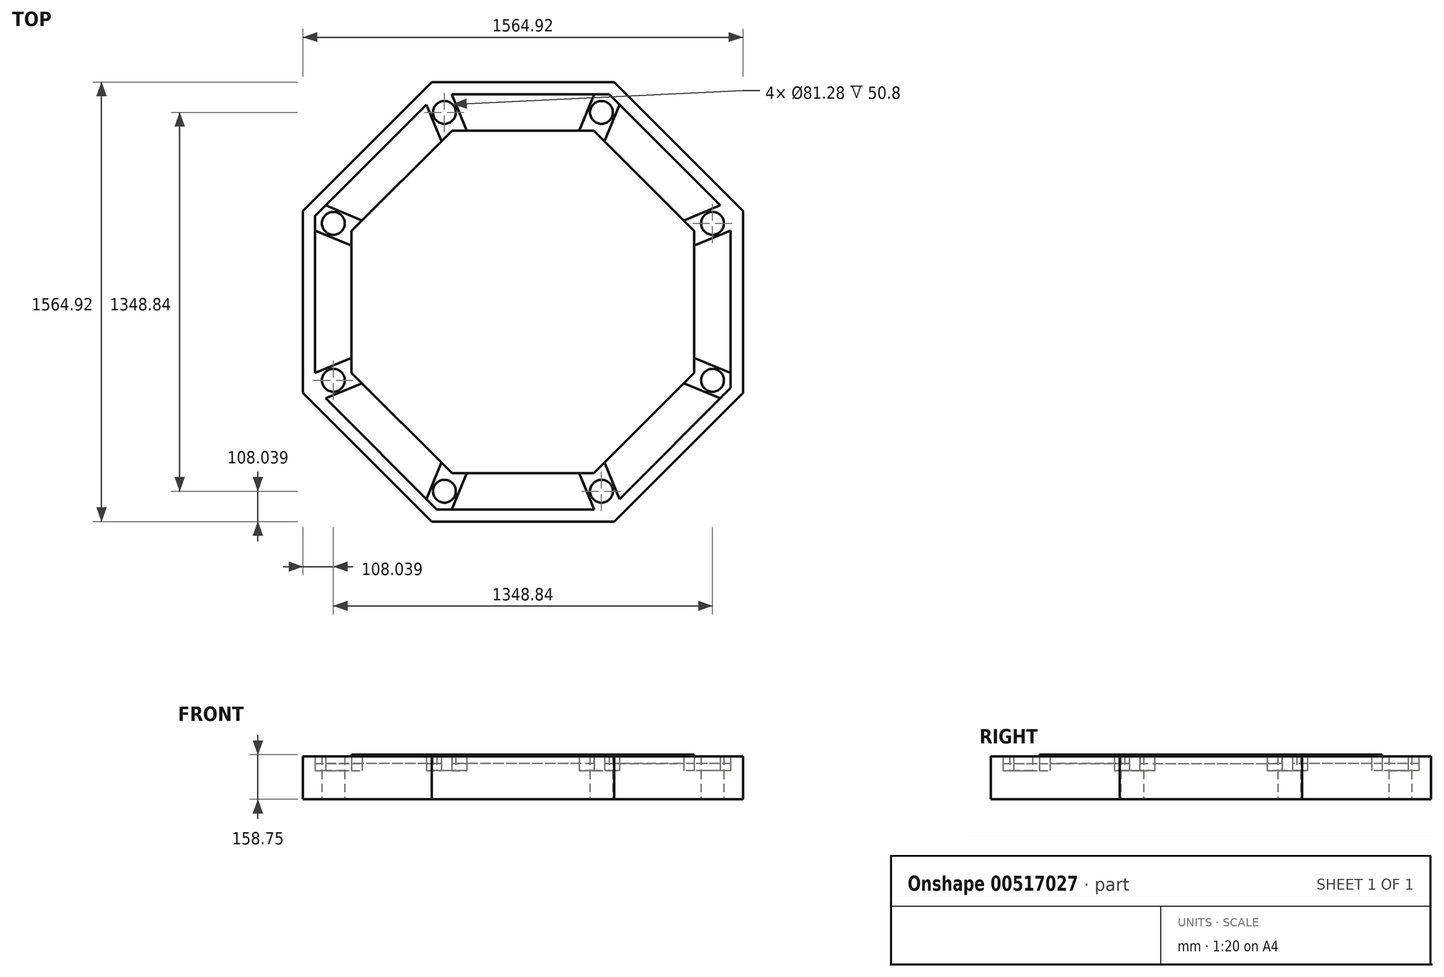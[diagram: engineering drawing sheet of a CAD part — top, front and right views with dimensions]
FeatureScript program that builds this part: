
annotation { "Feature Type Name" : "Feature", "Feature Type Description" : "" }
export const myFeature = defineFeature(function(context is Context, id is Id, definition is map)
    precondition{}
    {
        {
            var Q0;
            Q0=qCreatedBy(makeId("Top.planeOp"),FACE);
            var sketch = newSketch(context, id + "F0", { "sketchPlane" : qUnion([Q0])});
            skLineSegment(sketch, "E0.0", {"start": v(-324.1, 782.46) * mm, "end": v(324.1, 782.46) * mm});
            skLineSegment(sketch, "E0.1", {"start": v(324.1, 782.46) * mm, "end": v(782.46, 324.1) * mm});
            skLineSegment(sketch, "E0.2", {"start": v(782.46, 324.1) * mm, "end": v(782.46, -324.1) * mm});
            skLineSegment(sketch, "E0.3", {"start": v(782.46, -324.1) * mm, "end": v(324.1, -782.46) * mm});
            skLineSegment(sketch, "E0.4", {"start": v(324.1, -782.46) * mm, "end": v(-324.1, -782.46) * mm});
            skLineSegment(sketch, "E0.5", {"start": v(-324.1, -782.46) * mm, "end": v(-782.46, -324.1) * mm});
            skLineSegment(sketch, "E0.6", {"start": v(-782.46, -324.1) * mm, "end": v(-782.46, 324.1) * mm});
            skLineSegment(sketch, "E0.7", {"start": v(-782.46, 324.1) * mm, "end": v(-324.1, 782.46) * mm});
            skPoint(sketch, "E0.0.midPoint", {"position": v(0, 782.46) * mm});
            skLineSegment(sketch, "E1.0", {"start": v(-252.5, 609.6) * mm, "end": v(252.5, 609.6) * mm});
            skLineSegment(sketch, "E1.1", {"start": v(252.5, 609.6) * mm, "end": v(609.6, 252.5) * mm});
            skLineSegment(sketch, "E1.2", {"start": v(609.6, 252.5) * mm, "end": v(609.6, -252.5) * mm});
            skLineSegment(sketch, "E1.3", {"start": v(609.6, -252.5) * mm, "end": v(252.5, -609.6) * mm});
            skLineSegment(sketch, "E1.4", {"start": v(252.5, -609.6) * mm, "end": v(-252.5, -609.6) * mm});
            skLineSegment(sketch, "E1.5", {"start": v(-252.5, -609.6) * mm, "end": v(-609.6, -252.5) * mm});
            skLineSegment(sketch, "E1.6", {"start": v(-609.6, -252.5) * mm, "end": v(-609.6, 252.5) * mm});
            skLineSegment(sketch, "E1.7", {"start": v(-609.6, 252.5) * mm, "end": v(-252.5, 609.6) * mm});
            skPoint(sketch, "E1.0.midPoint", {"position": v(0, 609.6) * mm});
            skLineSegment(sketch, "E2.0", {"start": v(-306.2, 739.24) * mm, "end": v(306.2, 739.24) * mm});
            skLineSegment(sketch, "E2.1", {"start": v(306.2, 739.24) * mm, "end": v(739.24, 306.2) * mm});
            skLineSegment(sketch, "E2.2", {"start": v(739.24, 306.2) * mm, "end": v(739.24, -306.2) * mm});
            skLineSegment(sketch, "E2.3", {"start": v(739.24, -306.2) * mm, "end": v(306.2, -739.24) * mm});
            skLineSegment(sketch, "E2.4", {"start": v(306.2, -739.24) * mm, "end": v(-306.2, -739.24) * mm});
            skLineSegment(sketch, "E2.5", {"start": v(-306.2, -739.24) * mm, "end": v(-739.24, -306.2) * mm});
            skLineSegment(sketch, "E2.6", {"start": v(-739.24, -306.2) * mm, "end": v(-739.24, 306.2) * mm});
            skLineSegment(sketch, "E2.7", {"start": v(-739.24, 306.2) * mm, "end": v(-306.2, 739.24) * mm});
            skPoint(sketch, "E2.0.midPoint", {"position": v(0, 739.24) * mm});
            skLineSegment(sketch, "E3", {"start": v(-306.2, 739.24) * mm, "end": v(-252.5, 609.6) * mm, "construction": true});
            skLineSegment(sketch, "E4.0", {"start": v(-253.58, 739.24) * mm, "end": v(-199.88, 609.6) * mm});
            skLineSegment(sketch, "E5.0", {"start": v(-343.41, 702.03) * mm, "end": v(-289.71, 572.4) * mm});
            skLineSegment(sketch, "E6", {"start": v(0, 782.46) * mm, "end": v(0, -782.46) * mm, "construction": true});
            skCircle(sketch, "E7", {"center": v(-279.35, 674.42) * mm, "radius": 40.64 * mm});
            skLineSegment(sketch, "E8.MirrorCS", {"start": v(253.58, 739.24) * mm, "end": v(199.88, 609.6) * mm});
            skLineSegment(sketch, "E9.MirrorCS", {"start": v(343.41, 702.03) * mm, "end": v(289.71, 572.4) * mm});
            skCircle(sketch, "E10.MirrorC", {"center": v(279.35, 674.42) * mm, "radius": 40.64 * mm});
            skLineSegment(sketch, "E11", {"start": v(-782.46, 0) * mm, "end": v(782.46, 0) * mm, "construction": true});
            skLineSegment(sketch, "E12.MirrorCS", {"start": v(343.41, -702.03) * mm, "end": v(289.71, -572.4) * mm});
            skLineSegment(sketch, "E13.MirrorCS", {"start": v(253.58, -739.24) * mm, "end": v(199.88, -609.6) * mm});
            skCircle(sketch, "E14.MirrorC", {"center": v(279.35, -674.42) * mm, "radius": 40.64 * mm});
            skCircle(sketch, "E15.MirrorC", {"center": v(-279.35, -674.42) * mm, "radius": 40.64 * mm});
            skLineSegment(sketch, "E16.MirrorCS", {"start": v(-253.58, -739.24) * mm, "end": v(-199.88, -609.6) * mm});
            skLineSegment(sketch, "E17.MirrorCS", {"start": v(-343.41, -702.03) * mm, "end": v(-289.71, -572.4) * mm});
            skLineSegment(sketch, "E18", {"start": v(553.28, -553.28) * mm, "end": v(-553.28, 553.28) * mm, "construction": true});
            skLineSegment(sketch, "E19", {"start": v(553.28, 553.28) * mm, "end": v(-553.28, -553.28) * mm, "construction": true});
            skLineSegment(sketch, "E20.MirrorCS", {"start": v(702.03, 343.41) * mm, "end": v(572.4, 289.71) * mm});
            skLineSegment(sketch, "E21.MirrorCS", {"start": v(739.24, 253.58) * mm, "end": v(609.6, 199.88) * mm});
            skCircle(sketch, "E22.MirrorC", {"center": v(674.42, 279.35) * mm, "radius": 40.64 * mm});
            skLineSegment(sketch, "E23.MirrorCS", {"start": v(-739.24, -253.58) * mm, "end": v(-609.6, -199.88) * mm});
            skCircle(sketch, "E24.MirrorC", {"center": v(-674.42, -279.35) * mm, "radius": 40.64 * mm});
            skLineSegment(sketch, "E25.MirrorCS", {"start": v(-702.03, -343.41) * mm, "end": v(-572.4, -289.71) * mm});
            skLineSegment(sketch, "E26.MirrorCS", {"start": v(702.03, -343.41) * mm, "end": v(572.4, -289.71) * mm});
            skLineSegment(sketch, "E27.MirrorCS", {"start": v(739.24, -253.58) * mm, "end": v(609.6, -199.88) * mm});
            skCircle(sketch, "E28.MirrorC", {"center": v(674.42, -279.35) * mm, "radius": 40.64 * mm});
            skLineSegment(sketch, "E29.MirrorCS", {"start": v(-702.03, 343.41) * mm, "end": v(-572.4, 289.71) * mm});
            skLineSegment(sketch, "E30.MirrorCS", {"start": v(-739.24, 253.58) * mm, "end": v(-609.6, 199.88) * mm});
            skCircle(sketch, "E31.MirrorC", {"center": v(-674.42, 279.35) * mm, "radius": 40.64 * mm});
            skSolve(sketch);
        }
        {
            var Q0;
            Q0=makeQuery(id+"F0.imprint","IMPRINT",FACE,{"disambiguationData":[TD([[makeQuery(id+"F0.imprint","IMPRINT",EDGE,{"derivedFrom":sQuery(id+"F0.wireOp",EDGE,"E0.0")}),-1.0]])]});
            extrude(context, id + "F1", {"entities" : qUnion([Q0]), "endBound" : BoundingType.SYMMETRIC, "depth" : 152.4 * mm});
        }
        {
            var Q0;
            {var subQ0=sQuery(id+"F0.wireOp",EDGE,"E5.0");Q0=makeQuery(id+"F0.imprint","IMPRINT",FACE,{"disambiguationData":[TD([[makeQuery(id+"F0.imprint","IMPRINT",EDGE,{"derivedFrom":subQ0}),-1.0]])]});}
            var Q1;
            {var subQ0=sQuery(id+"F0.wireOp",EDGE,"E4.0");Q1=makeQuery(id+"F0.imprint","IMPRINT",FACE,{"disambiguationData":[TD([[makeQuery(id+"F0.imprint","IMPRINT",EDGE,{"derivedFrom":subQ0}),1.0]])]});}
            var Q2;
            {var subQ0=sQuery(id+"F0.wireOp",EDGE,"E9.MirrorCS");Q2=makeQuery(id+"F0.imprint","IMPRINT",FACE,{"disambiguationData":[TD([[makeQuery(id+"F0.imprint","IMPRINT",EDGE,{"derivedFrom":subQ0}),1.0]])]});}
            var Q3;
            {var subQ0=sQuery(id+"F0.wireOp",EDGE,"E23.MirrorCS");Q3=makeQuery(id+"F0.imprint","IMPRINT",FACE,{"disambiguationData":[TD([[makeQuery(id+"F0.imprint","IMPRINT",EDGE,{"derivedFrom":subQ0}),1.0]])]});}
            var Q4;
            {var subQ0=sQuery(id+"F0.wireOp",EDGE,"E21.MirrorCS");Q4=makeQuery(id+"F0.imprint","IMPRINT",FACE,{"disambiguationData":[TD([[makeQuery(id+"F0.imprint","IMPRINT",EDGE,{"derivedFrom":subQ0}),1.0]])]});}
            var Q5;
            {var subQ0=sQuery(id+"F0.wireOp",EDGE,"E12.MirrorCS");Q5=makeQuery(id+"F0.imprint","IMPRINT",FACE,{"disambiguationData":[TD([[makeQuery(id+"F0.imprint","IMPRINT",EDGE,{"derivedFrom":subQ0}),-1.0]])]});}
            var Q6;
            {var subQ0=sQuery(id+"F0.wireOp",EDGE,"E13.MirrorCS");Q6=makeQuery(id+"F0.imprint","IMPRINT",FACE,{"disambiguationData":[TD([[makeQuery(id+"F0.imprint","IMPRINT",EDGE,{"derivedFrom":subQ0}),1.0]])]});}
            var Q7;
            {var subQ0=sQuery(id+"F0.wireOp",EDGE,"E17.MirrorCS");Q7=makeQuery(id+"F0.imprint","IMPRINT",FACE,{"disambiguationData":[TD([[makeQuery(id+"F0.imprint","IMPRINT",EDGE,{"derivedFrom":subQ0}),1.0]])]});}
            extrude(context, id + "F2", {"entities" : qUnion([Q0, Q1, Q2, Q3, Q4, Q5, Q6, Q7]), "operationType" : NewBodyOperationType.ADD, "endBound" : BoundingType.SYMMETRIC, "depth" : 127 * mm});
        }
        {
            var Q0;
            Q0=makeQuery(id+"F2.opExtrude","CAP_FACE",FACE,{"disambiguationData":[OSD([sQuery(id+"F0.wireOp",EDGE,"E1.3"),sQuery(id+"F0.wireOp",EDGE,"E2.3"),sQuery(id+"F0.wireOp",EDGE,"E12.MirrorCS"),sQuery(id+"F0.wireOp",EDGE,"E26.MirrorCS")])],"isStart":true});
            var Q1;
            Q1=makeQuery(id+"F2.opExtrude","CAP_FACE",FACE,{"disambiguationData":[OSD([sQuery(id+"F0.wireOp",EDGE,"E1.4"),sQuery(id+"F0.wireOp",EDGE,"E2.4"),sQuery(id+"F0.wireOp",EDGE,"E13.MirrorCS"),sQuery(id+"F0.wireOp",EDGE,"E16.MirrorCS")])],"isStart":true});
            var Q2;
            Q2=makeQuery(id+"F2.opExtrude","CAP_FACE",FACE,{"disambiguationData":[OSD([sQuery(id+"F0.wireOp",EDGE,"E1.5"),sQuery(id+"F0.wireOp",EDGE,"E2.5"),sQuery(id+"F0.wireOp",EDGE,"E17.MirrorCS"),sQuery(id+"F0.wireOp",EDGE,"E25.MirrorCS")])],"isStart":true});
            var Q3;
            Q3=makeQuery(id+"F2.opExtrude","CAP_FACE",FACE,{"disambiguationData":[OSD([sQuery(id+"F0.wireOp",EDGE,"E1.6"),sQuery(id+"F0.wireOp",EDGE,"E2.6"),sQuery(id+"F0.wireOp",EDGE,"E23.MirrorCS"),sQuery(id+"F0.wireOp",EDGE,"E30.MirrorCS")])],"isStart":true});
            var Q4;
            Q4=makeQuery(id+"F2.opExtrude","CAP_FACE",FACE,{"disambiguationData":[OSD([sQuery(id+"F0.wireOp",EDGE,"E1.7"),sQuery(id+"F0.wireOp",EDGE,"E2.7"),sQuery(id+"F0.wireOp",EDGE,"E5.0"),sQuery(id+"F0.wireOp",EDGE,"E29.MirrorCS")])],"isStart":true});
            var Q5;
            Q5=makeQuery(id+"F2.opExtrude","CAP_FACE",FACE,{"disambiguationData":[OSD([sQuery(id+"F0.wireOp",EDGE,"E1.0"),sQuery(id+"F0.wireOp",EDGE,"E2.0"),sQuery(id+"F0.wireOp",EDGE,"E4.0"),sQuery(id+"F0.wireOp",EDGE,"E8.MirrorCS")])],"isStart":true});
            var Q6;
            Q6=makeQuery(id+"F2.opExtrude","CAP_FACE",FACE,{"disambiguationData":[OSD([sQuery(id+"F0.wireOp",EDGE,"E1.1"),sQuery(id+"F0.wireOp",EDGE,"E2.1"),sQuery(id+"F0.wireOp",EDGE,"E9.MirrorCS"),sQuery(id+"F0.wireOp",EDGE,"E20.MirrorCS")])],"isStart":true});
            var Q7;
            Q7=makeQuery(id+"F2.opExtrude","CAP_FACE",FACE,{"disambiguationData":[OSD([sQuery(id+"F0.wireOp",EDGE,"E1.2"),sQuery(id+"F0.wireOp",EDGE,"E2.2"),sQuery(id+"F0.wireOp",EDGE,"E21.MirrorCS"),sQuery(id+"F0.wireOp",EDGE,"E27.MirrorCS")])],"isStart":true});
            extrude(context, id + "F3", {"entities" : qUnion([Q0, Q1, Q2, Q3, Q4, Q5, Q6, Q7]), "operationType" : NewBodyOperationType.ADD, "depth" : 12.7 * mm});
        }
        {
            var Q0;
            {var subQ4=sQuery(id+"F0.wireOp",EDGE,"E4.0");Q0=makeQuery(id+"F0.imprint","IMPRINT",FACE,{"disambiguationData":[TD([[makeQuery(id+"F0.imprint","IMPRINT",EDGE,{"derivedFrom":subQ4}),-1.0]])]});}
            var Q1;
            {var subQ3=sQuery(id+"F0.wireOp",EDGE,"E8.MirrorCS");Q1=makeQuery(id+"F0.imprint","IMPRINT",FACE,{"disambiguationData":[TD([[makeQuery(id+"F0.imprint","IMPRINT",EDGE,{"derivedFrom":subQ3}),1.0]])]});}
            var Q2;
            {var subQ7=sQuery(id+"F0.wireOp",EDGE,"E29.MirrorCS");Q2=makeQuery(id+"F0.imprint","IMPRINT",FACE,{"disambiguationData":[TD([[makeQuery(id+"F0.imprint","IMPRINT",EDGE,{"derivedFrom":subQ7}),-1.0]])]});}
            var Q3;
            {var subQ4=sQuery(id+"F0.wireOp",EDGE,"E23.MirrorCS");Q3=makeQuery(id+"F0.imprint","IMPRINT",FACE,{"disambiguationData":[TD([[makeQuery(id+"F0.imprint","IMPRINT",EDGE,{"derivedFrom":subQ4}),-1.0]])]});}
            var Q4;
            {var subQ3=sQuery(id+"F0.wireOp",EDGE,"E20.MirrorCS");Q4=makeQuery(id+"F0.imprint","IMPRINT",FACE,{"disambiguationData":[TD([[makeQuery(id+"F0.imprint","IMPRINT",EDGE,{"derivedFrom":subQ3}),1.0]])]});}
            var Q5;
            {var subQ7=sQuery(id+"F0.wireOp",EDGE,"E26.MirrorCS");Q5=makeQuery(id+"F0.imprint","IMPRINT",FACE,{"disambiguationData":[TD([[makeQuery(id+"F0.imprint","IMPRINT",EDGE,{"derivedFrom":subQ7}),-1.0]])]});}
            var Q6;
            Q6=makeQuery(id+"F0.imprint","IMPRINT",FACE,{"disambiguationData":[TD([[makeQuery(id+"F0.imprint","IMPRINT",EDGE,{"derivedFrom":sQuery(id+"F0.wireOp",EDGE,"E15.MirrorC")}),1.0]])]});
            var Q7;
            {var subQ3=sQuery(id+"F0.wireOp",EDGE,"E12.MirrorCS");Q7=makeQuery(id+"F0.imprint","IMPRINT",FACE,{"disambiguationData":[TD([[makeQuery(id+"F0.imprint","IMPRINT",EDGE,{"derivedFrom":subQ3}),1.0]])]});}
            var Q8;
            Q8=makeQuery(id+"F0.imprint","IMPRINT",FACE,{"disambiguationData":[TD([[makeQuery(id+"F0.imprint","IMPRINT",EDGE,{"derivedFrom":sQuery(id+"F0.wireOp",EDGE,"E22.MirrorC")}),1.0]])]});
            var Q9;
            Q9=makeQuery(id+"F0.imprint","IMPRINT",FACE,{"disambiguationData":[TD([[makeQuery(id+"F0.imprint","IMPRINT",EDGE,{"derivedFrom":sQuery(id+"F0.wireOp",EDGE,"E10.MirrorC")}),-1.0]])]});
            var Q10;
            Q10=makeQuery(id+"F0.imprint","IMPRINT",FACE,{"disambiguationData":[TD([[makeQuery(id+"F0.imprint","IMPRINT",EDGE,{"derivedFrom":sQuery(id+"F0.wireOp",EDGE,"E7")}),1.0]])]});
            var Q11;
            Q11=makeQuery(id+"F0.imprint","IMPRINT",FACE,{"disambiguationData":[TD([[makeQuery(id+"F0.imprint","IMPRINT",EDGE,{"derivedFrom":sQuery(id+"F0.wireOp",EDGE,"E31.MirrorC")}),-1.0]])]});
            var Q12;
            Q12=makeQuery(id+"F0.imprint","IMPRINT",FACE,{"disambiguationData":[TD([[makeQuery(id+"F0.imprint","IMPRINT",EDGE,{"derivedFrom":sQuery(id+"F0.wireOp",EDGE,"E24.MirrorC")}),1.0]])]});
            var Q13;
            Q13=makeQuery(id+"F0.imprint","IMPRINT",FACE,{"disambiguationData":[TD([[makeQuery(id+"F0.imprint","IMPRINT",EDGE,{"derivedFrom":sQuery(id+"F0.wireOp",EDGE,"E15.MirrorC")}),-1.0]])]});
            var Q14;
            Q14=makeQuery(id+"F0.imprint","IMPRINT",FACE,{"disambiguationData":[TD([[makeQuery(id+"F0.imprint","IMPRINT",EDGE,{"derivedFrom":sQuery(id+"F0.wireOp",EDGE,"E14.MirrorC")}),1.0]])]});
            var Q15;
            Q15=makeQuery(id+"F0.imprint","IMPRINT",FACE,{"disambiguationData":[TD([[makeQuery(id+"F0.imprint","IMPRINT",EDGE,{"derivedFrom":sQuery(id+"F0.wireOp",EDGE,"E28.MirrorC")}),-1.0]])]});
            extrude(context, id + "F4", {"entities" : qUnion([Q0, Q1, Q2, Q3, Q4, Q5, Q6, Q7, Q8, Q9, Q10, Q11, Q12, Q13, Q14, Q15]), "operationType" : NewBodyOperationType.ADD, "endBound" : BoundingType.SYMMETRIC, "depth" : 152.4 * mm});
        }
        {
            var Q0;
            Q0=makeQuery(id+"F0.imprint","IMPRINT",FACE,{"disambiguationData":[TD([[makeQuery(id+"F0.imprint","IMPRINT",EDGE,{"derivedFrom":sQuery(id+"F0.wireOp",EDGE,"E31.MirrorC")}),-1.0]])]});
            var Q1;
            Q1=makeQuery(id+"F0.imprint","IMPRINT",FACE,{"disambiguationData":[TD([[makeQuery(id+"F0.imprint","IMPRINT",EDGE,{"derivedFrom":sQuery(id+"F0.wireOp",EDGE,"E7")}),1.0]])]});
            var Q2;
            Q2=makeQuery(id+"F0.imprint","IMPRINT",FACE,{"disambiguationData":[TD([[makeQuery(id+"F0.imprint","IMPRINT",EDGE,{"derivedFrom":sQuery(id+"F0.wireOp",EDGE,"E10.MirrorC")}),-1.0]])]});
            var Q3;
            Q3=makeQuery(id+"F0.imprint","IMPRINT",FACE,{"disambiguationData":[TD([[makeQuery(id+"F0.imprint","IMPRINT",EDGE,{"derivedFrom":sQuery(id+"F0.wireOp",EDGE,"E22.MirrorC")}),1.0]])]});
            var Q4;
            Q4=makeQuery(id+"F0.imprint","IMPRINT",FACE,{"disambiguationData":[TD([[makeQuery(id+"F0.imprint","IMPRINT",EDGE,{"derivedFrom":sQuery(id+"F0.wireOp",EDGE,"E28.MirrorC")}),-1.0]])]});
            var Q5;
            Q5=makeQuery(id+"F0.imprint","IMPRINT",FACE,{"disambiguationData":[TD([[makeQuery(id+"F0.imprint","IMPRINT",EDGE,{"derivedFrom":sQuery(id+"F0.wireOp",EDGE,"E14.MirrorC")}),1.0]])]});
            var Q6;
            Q6=makeQuery(id+"F0.imprint","IMPRINT",FACE,{"disambiguationData":[TD([[makeQuery(id+"F0.imprint","IMPRINT",EDGE,{"derivedFrom":sQuery(id+"F0.wireOp",EDGE,"E15.MirrorC")}),-1.0]])]});
            var Q7;
            Q7=makeQuery(id+"F0.imprint","IMPRINT",FACE,{"disambiguationData":[TD([[makeQuery(id+"F0.imprint","IMPRINT",EDGE,{"derivedFrom":sQuery(id+"F0.wireOp",EDGE,"E24.MirrorC")}),1.0]])]});
            extrude(context, id + "F5", {"entities" : qUnion([Q0, Q1, Q2, Q3, Q4, Q5, Q6, Q7]), "operationType" : NewBodyOperationType.REMOVE, "endBound" : BoundingType.THROUGH_ALL, "depth" : 50.8 * mm});
        }
        {
            var Q0;
            Q0=makeQuery(id+"F0.imprint","IMPRINT",FACE,{"disambiguationData":[TD([[makeQuery(id+"F0.imprint","IMPRINT",EDGE,{"derivedFrom":sQuery(id+"F0.wireOp",EDGE,"E7")}),1.0]])]});
            var Q1;
            Q1=makeQuery(id+"F0.imprint","IMPRINT",FACE,{"disambiguationData":[TD([[makeQuery(id+"F0.imprint","IMPRINT",EDGE,{"derivedFrom":sQuery(id+"F0.wireOp",EDGE,"E10.MirrorC")}),-1.0]])]});
            var Q2;
            Q2=makeQuery(id+"F0.imprint","IMPRINT",FACE,{"disambiguationData":[TD([[makeQuery(id+"F0.imprint","IMPRINT",EDGE,{"derivedFrom":sQuery(id+"F0.wireOp",EDGE,"E22.MirrorC")}),1.0]])]});
            var Q3;
            Q3=makeQuery(id+"F0.imprint","IMPRINT",FACE,{"disambiguationData":[TD([[makeQuery(id+"F0.imprint","IMPRINT",EDGE,{"derivedFrom":sQuery(id+"F0.wireOp",EDGE,"E28.MirrorC")}),-1.0]])]});
            var Q4;
            Q4=makeQuery(id+"F0.imprint","IMPRINT",FACE,{"disambiguationData":[TD([[makeQuery(id+"F0.imprint","IMPRINT",EDGE,{"derivedFrom":sQuery(id+"F0.wireOp",EDGE,"E14.MirrorC")}),1.0]])]});
            var Q5;
            Q5=makeQuery(id+"F0.imprint","IMPRINT",FACE,{"disambiguationData":[TD([[makeQuery(id+"F0.imprint","IMPRINT",EDGE,{"derivedFrom":sQuery(id+"F0.wireOp",EDGE,"E15.MirrorC")}),-1.0]])]});
            var Q6;
            Q6=makeQuery(id+"F0.imprint","IMPRINT",FACE,{"disambiguationData":[TD([[makeQuery(id+"F0.imprint","IMPRINT",EDGE,{"derivedFrom":sQuery(id+"F0.wireOp",EDGE,"E24.MirrorC")}),1.0]])]});
            var Q7;
            Q7=makeQuery(id+"F0.imprint","IMPRINT",FACE,{"disambiguationData":[TD([[makeQuery(id+"F0.imprint","IMPRINT",EDGE,{"derivedFrom":sQuery(id+"F0.wireOp",EDGE,"E31.MirrorC")}),-1.0]])]});
            extrude(context, id + "F6", {"entities" : qUnion([Q0, Q1, Q2, Q3, Q4, Q5, Q6, Q7]), "operationType" : NewBodyOperationType.ADD, "depth" : 25.4 * mm});
        }
        {
            var Q0;
            {var subQ0=sQuery(id+"F0.wireOp",EDGE,"E1.7");var subQ19=sQuery(id+"F0.wireOp",EDGE,"E1.0");var subQ24=makeQuery(id+"F0.imprint","INTERSECT",VERTEX,{"derivedFrom":[subQ19,subQ0]});Q0=makeQuery(id+"F0.imprint","IMPRINT",FACE,{"disambiguationData":[TD([[makeQuery(id+"F0.imprint","IMPRINT",EDGE,{"disambiguationData":[TD([[subQ24,-1.0]])],"derivedFrom":subQ19}),-1.0]])]});}
            extrude(context, id + "F7", {"entities" : qUnion([Q0]), "operationType" : NewBodyOperationType.ADD, "oppositeDirection" : true, "depth" : 76.2 * mm});
        }
        {
            var Q0;
            {var subQ0=sQuery(id+"F0.wireOp",EDGE,"E1.7");var subQ19=sQuery(id+"F0.wireOp",EDGE,"E1.0");var subQ24=makeQuery(id+"F0.imprint","INTERSECT",VERTEX,{"derivedFrom":[subQ19,subQ0]});Q0=makeQuery(id+"F0.imprint","IMPRINT",FACE,{"disambiguationData":[TD([[makeQuery(id+"F0.imprint","IMPRINT",EDGE,{"disambiguationData":[TD([[subQ24,-1.0]])],"derivedFrom":subQ19}),-1.0]])]});}
            extrude(context, id + "F8", {"entities" : qUnion([Q0]), "operationType" : NewBodyOperationType.ADD, "depth" : 82.55 * mm});
        }
        {
            var Q0;
            Q0=makeQuery(id+"F2.opExtrude","CAP_FACE",FACE,{"disambiguationData":[OSD([sQuery(id+"F0.wireOp",EDGE,"E1.4"),sQuery(id+"F0.wireOp",EDGE,"E2.4"),sQuery(id+"F0.wireOp",EDGE,"E13.MirrorCS"),sQuery(id+"F0.wireOp",EDGE,"E16.MirrorCS")])],"isStart":false});
            var Q1;
            Q1=makeQuery(id+"F2.opExtrude","CAP_FACE",FACE,{"disambiguationData":[OSD([sQuery(id+"F0.wireOp",EDGE,"E1.3"),sQuery(id+"F0.wireOp",EDGE,"E2.3"),sQuery(id+"F0.wireOp",EDGE,"E12.MirrorCS"),sQuery(id+"F0.wireOp",EDGE,"E26.MirrorCS")])],"isStart":false});
            var Q2;
            Q2=makeQuery(id+"F2.opExtrude","CAP_FACE",FACE,{"disambiguationData":[OSD([sQuery(id+"F0.wireOp",EDGE,"E1.2"),sQuery(id+"F0.wireOp",EDGE,"E2.2"),sQuery(id+"F0.wireOp",EDGE,"E21.MirrorCS"),sQuery(id+"F0.wireOp",EDGE,"E27.MirrorCS")])],"isStart":false});
            var Q3;
            Q3=makeQuery(id+"F2.opExtrude","CAP_FACE",FACE,{"disambiguationData":[OSD([sQuery(id+"F0.wireOp",EDGE,"E1.1"),sQuery(id+"F0.wireOp",EDGE,"E2.1"),sQuery(id+"F0.wireOp",EDGE,"E9.MirrorCS"),sQuery(id+"F0.wireOp",EDGE,"E20.MirrorCS")])],"isStart":false});
            var Q4;
            Q4=makeQuery(id+"F2.opExtrude","CAP_FACE",FACE,{"disambiguationData":[OSD([sQuery(id+"F0.wireOp",EDGE,"E1.0"),sQuery(id+"F0.wireOp",EDGE,"E2.0"),sQuery(id+"F0.wireOp",EDGE,"E4.0"),sQuery(id+"F0.wireOp",EDGE,"E8.MirrorCS")])],"isStart":false});
            var Q5;
            Q5=makeQuery(id+"F2.opExtrude","CAP_FACE",FACE,{"disambiguationData":[OSD([sQuery(id+"F0.wireOp",EDGE,"E1.7"),sQuery(id+"F0.wireOp",EDGE,"E2.7"),sQuery(id+"F0.wireOp",EDGE,"E5.0"),sQuery(id+"F0.wireOp",EDGE,"E29.MirrorCS")])],"isStart":false});
            var Q6;
            Q6=makeQuery(id+"F2.opExtrude","CAP_FACE",FACE,{"disambiguationData":[OSD([sQuery(id+"F0.wireOp",EDGE,"E1.6"),sQuery(id+"F0.wireOp",EDGE,"E2.6"),sQuery(id+"F0.wireOp",EDGE,"E23.MirrorCS"),sQuery(id+"F0.wireOp",EDGE,"E30.MirrorCS")])],"isStart":false});
            var Q7;
            Q7=makeQuery(id+"F2.opExtrude","CAP_FACE",FACE,{"disambiguationData":[OSD([sQuery(id+"F0.wireOp",EDGE,"E1.5"),sQuery(id+"F0.wireOp",EDGE,"E2.5"),sQuery(id+"F0.wireOp",EDGE,"E17.MirrorCS"),sQuery(id+"F0.wireOp",EDGE,"E25.MirrorCS")])],"isStart":false});
            extrude(context, id + "F9", {"entities" : qUnion([Q0, Q1, Q2, Q3, Q4, Q5, Q6, Q7]), "operationType" : NewBodyOperationType.REMOVE, "oppositeDirection" : true, "depth" : 12.7 * mm, "offsetDistance" : 25.4 * mm});
        }
    });
